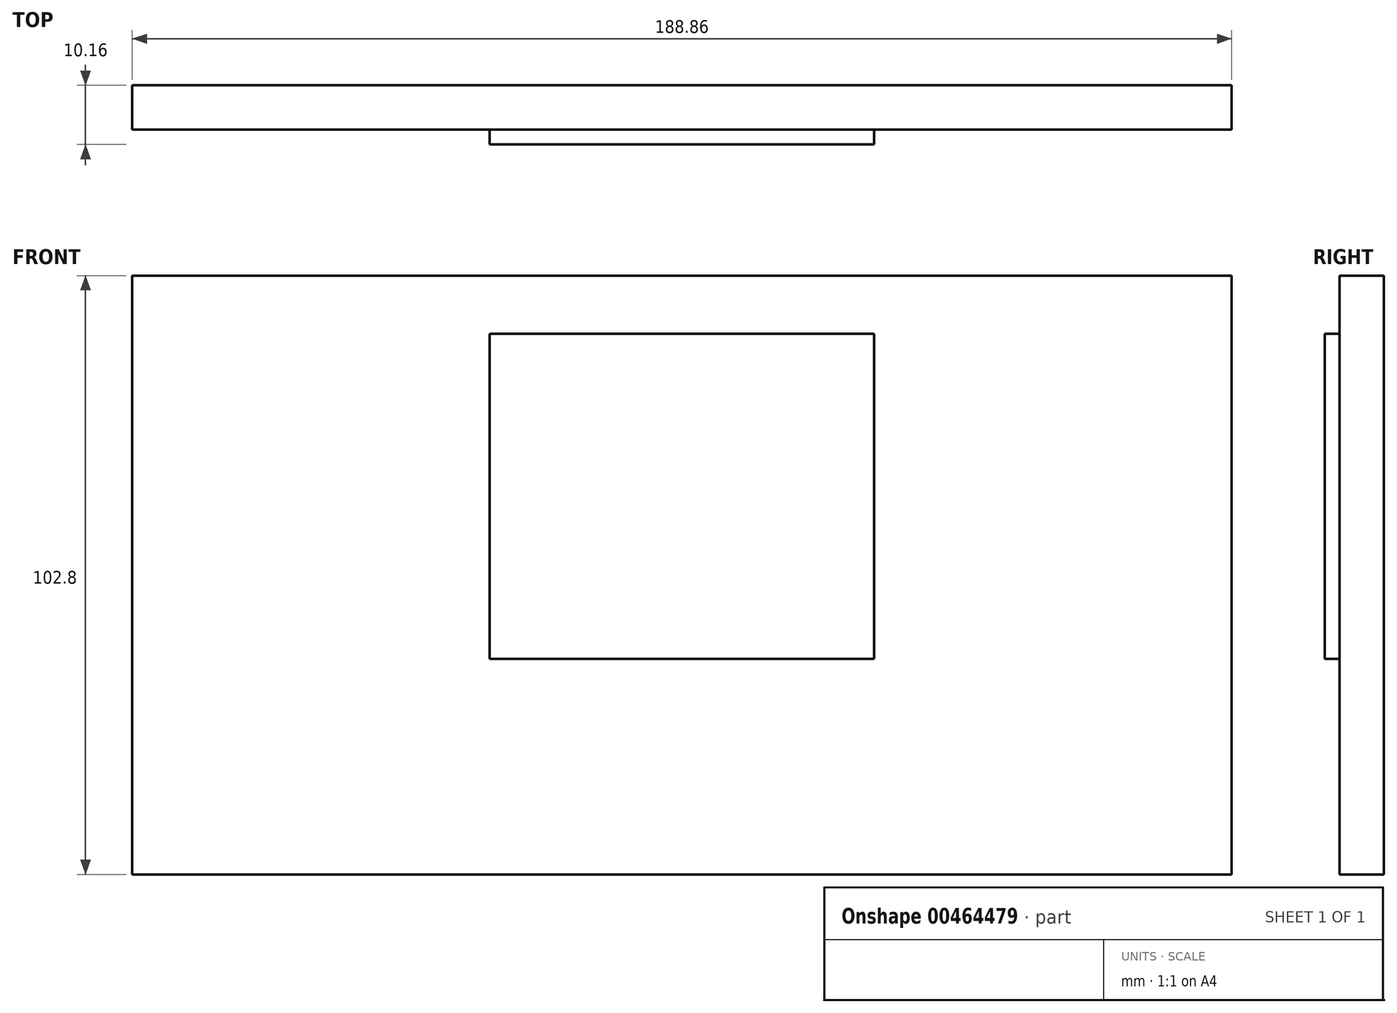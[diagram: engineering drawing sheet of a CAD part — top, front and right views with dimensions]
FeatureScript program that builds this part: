
annotation { "Feature Type Name" : "Feature", "Feature Type Description" : "" }
export const myFeature = defineFeature(function(context is Context, id is Id, definition is map)
    precondition{}
    {
        {
            var Q0;
            Q0=qCreatedBy(makeId("Front.planeOp"),FACE);
            var sketch = newSketch(context, id + "F0", { "sketchPlane" : qUnion([Q0])});
            skLineSegment(sketch, "E0.bottom", {"start": v(-94.43, 51.4) * mm, "end": v(94.43, 51.4) * mm});
            skLineSegment(sketch, "E0.top", {"start": v(-94.43, -51.4) * mm, "end": v(94.43, -51.4) * mm});
            skLineSegment(sketch, "E0.left", {"start": v(-94.43, 51.4) * mm, "end": v(-94.43, -51.4) * mm});
            skLineSegment(sketch, "E0.right", {"start": v(94.43, 51.4) * mm, "end": v(94.43, -51.4) * mm});
            skPoint(sketch, "E0.middle", {"position": v(0, 0) * mm});
            skSolve(sketch);
        }
        {
            var Q0;
            Q0=makeQuery(id+"F0.imprint","IMPRINT",FACE,{"disambiguationData":[TD([[makeQuery(id+"F0.imprint","IMPRINT",EDGE,{"derivedFrom":sQuery(id+"F0.wireOp",EDGE,"E0.bottom")}),-1.0]])]});
            extrude(context, id + "F1", {"entities" : qUnion([Q0]), "depth" : 7.62 * mm});
        }
        {
            var Q0;
            Q0=qCreatedBy(makeId("Front.planeOp"),FACE);
            var sketch = newSketch(context, id + "F2", { "sketchPlane" : qUnion([Q0])});
            skLineSegment(sketch, "E1.bottom", {"start": v(-33.03, -14.42) * mm, "end": v(33.03, -14.42) * mm});
            skLineSegment(sketch, "E1.top", {"start": v(-33.03, 41.4) * mm, "end": v(33.03, 41.4) * mm});
            skLineSegment(sketch, "E1.left", {"start": v(-33.03, -14.42) * mm, "end": v(-33.03, 41.4) * mm});
            skLineSegment(sketch, "E1.right", {"start": v(33.03, -14.42) * mm, "end": v(33.03, 41.4) * mm});
            skPoint(sketch, "E1.middle", {"position": v(0, 13.5) * mm});
            skSolve(sketch);
        }
        {
            var Q0;
            Q0 = qSketchRegion(id + "F2", true);
            extrude(context, id + "F3", {"entities" : qUnion([Q0]), "operationType" : NewBodyOperationType.ADD, "depth" : 10.16 * mm});
        }
    });
